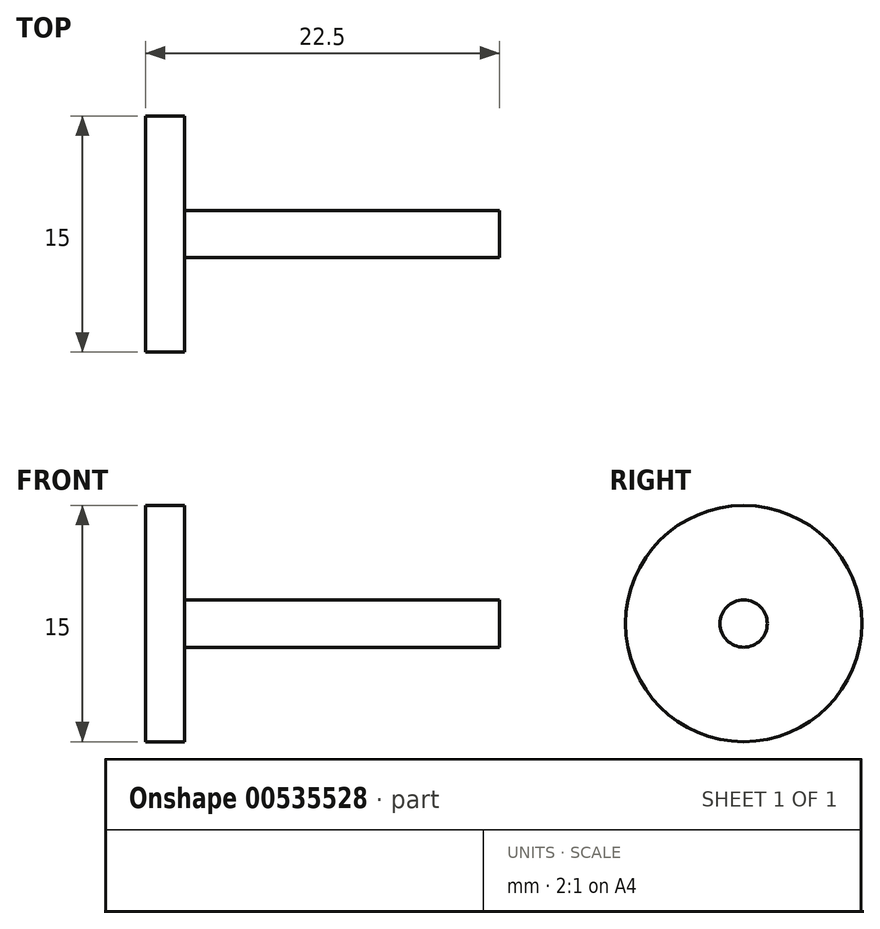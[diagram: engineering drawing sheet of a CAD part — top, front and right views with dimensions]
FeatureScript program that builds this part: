
annotation { "Feature Type Name" : "Feature", "Feature Type Description" : "" }
export const myFeature = defineFeature(function(context is Context, id is Id, definition is map)
    precondition{}
    {
        {
            var Q0;
            Q0=qCreatedBy(makeId("Right.planeOp"),FACE);
            var sketch = newSketch(context, id + "F0", { "sketchPlane" : qUnion([Q0])});
            skCircle(sketch, "E0", {"center": v(0, 0) * mm, "radius": 1.5 * mm});
            skSolve(sketch);
        }
        {
            var Q0;
            Q0 = qSketchRegion(id + "F0", true);
            extrude(context, id + "F1", {"entities" : qUnion([Q0]), "depth" : 20 * mm, "offsetDistance" : 25 * mm});
        }
        {
            var Q0;
            Q0=makeQuery(id+"F1.opExtrude","CAP_FACE",FACE,{"disambiguationData":[OSD([sQuery(id+"F0.wireOp",EDGE,"E0")])],"isStart":true});
            var sketch = newSketch(context, id + "F2", { "sketchPlane" : qUnion([Q0])});
            skCircle(sketch, "E1", {"center": v(0, 0) * mm, "radius": 7.5 * mm});
            skSolve(sketch);
        }
        {
            var Q0;
            Q0 = qSketchRegion(id + "F2", true);
            extrude(context, id + "F3", {"entities" : qUnion([Q0]), "operationType" : NewBodyOperationType.ADD, "depth" : 2.5 * mm, "offsetDistance" : 25 * mm});
        }
    });
